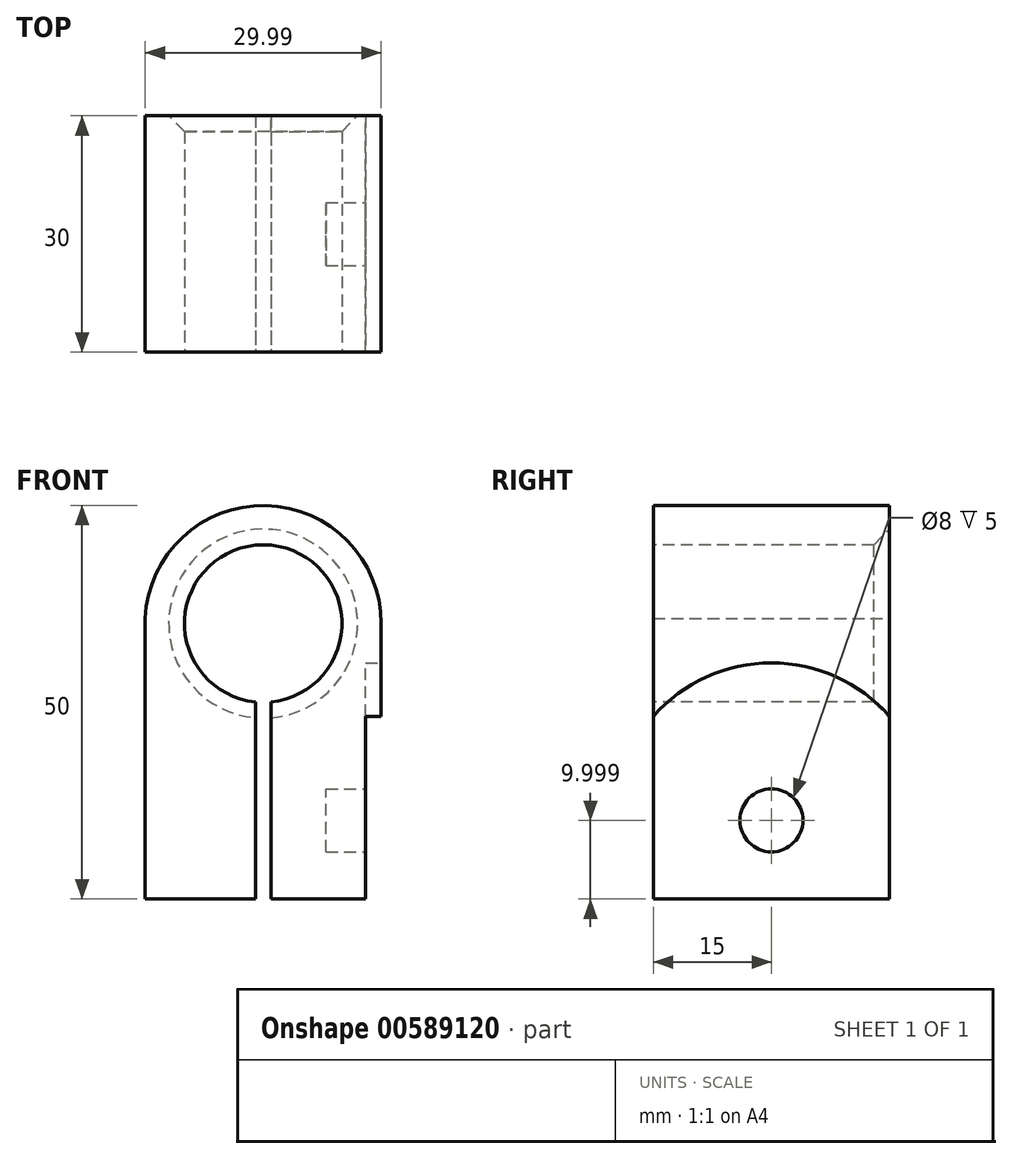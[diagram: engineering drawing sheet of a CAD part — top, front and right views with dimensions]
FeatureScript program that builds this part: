
annotation { "Feature Type Name" : "Feature", "Feature Type Description" : "" }
export const myFeature = defineFeature(function(context is Context, id is Id, definition is map)
    precondition{}
    {
        {
            var Q0;
            Q0=qCreatedBy(makeId("Front.planeOp"),FACE);
            var sketch = newSketch(context, id + "F0", { "sketchPlane" : qUnion([Q0])});
            skLineSegment(sketch, "E0", {"start": v(-14.99, -24.4) * mm, "end": v(-0.99, -24.4) * mm});
            skLineSegment(sketch, "E1", {"start": v(-24.44, 10.6) * mm, "end": v(37.77, 10.6) * mm, "construction": true});
            skLineSegment(sketch, "E2.trimOffspring", {"start": v(1, -24.4) * mm, "end": v(15, -24.4) * mm});
            skLineSegment(sketch, "E3", {"start": v(-14.99, -24.4) * mm, "end": v(-14.99, 11.27) * mm});
            skLineSegment(sketch, "E4", {"start": v(15, -24.4) * mm, "end": v(15, 10.6) * mm});
            skArc(sketch, "E5.trimOffspring", {"start": v(15, 10.6) * mm, "mid": v(0.33, 25.6) * mm, "end": v(-14.99, 11.27) * mm});
            skLineSegment(sketch, "E6", {"start": v(-0.99, -24.4) * mm, "end": v(1, -24.4) * mm});
            skSolve(sketch);
        }
        {
            var Q0;
            Q0 = qSketchRegion(id + "F0", true);
            extrude(context, id + "F1", {"entities" : qUnion([Q0]), "depth" : 30 * mm, "offsetDistance" : 25 * mm});
        }
        {
            var Q0;
            Q0=makeQuery(id+"F1.opExtrude","CAP_FACE",FACE,{"disambiguationData":[OSD([sQuery(id+"F0.wireOp",EDGE,"E0"),sQuery(id+"F0.wireOp",EDGE,"E2.trimOffspring"),sQuery(id+"F0.wireOp",EDGE,"E3"),sQuery(id+"F0.wireOp",EDGE,"E4"),sQuery(id+"F0.wireOp",EDGE,"E5.trimOffspring"),sQuery(id+"F0.wireOp",EDGE,"E6")])],"isStart":false});
            var sketch = newSketch(context, id + "F2", { "sketchPlane" : qUnion([Q0])});
            skLineSegment(sketch, "E7", {"start": v(-23.35, -24.4) * mm, "end": v(31.91, -24.4) * mm, "construction": true});
            skLineSegment(sketch, "E8", {"start": v(-20.4, 10.6) * mm, "end": v(33.94, 10.6) * mm, "construction": true});
            skLineSegment(sketch, "E9", {"start": v(0, -24.4) * mm, "end": v(0, 32.16) * mm, "construction": true});
            skCircle(sketch, "E10", {"center": v(0, 10.6) * mm, "radius": 10 * mm});
            skSolve(sketch);
        }
        {
            var Q0;
            Q0=makeQuery(id+"F2.imprint","IMPRINT",FACE,{"disambiguationData":[TD([[makeQuery(id+"F2.imprint","IMPRINT",EDGE,{"derivedFrom":sQuery(id+"F2.wireOp",EDGE,"E10")}),1.0]])]});
            extrude(context, id + "F3", {"entities" : qUnion([Q0]), "operationType" : NewBodyOperationType.REMOVE, "endBound" : BoundingType.THROUGH_ALL, "oppositeDirection" : true, "depth" : 25 * mm, "offsetDistance" : 25 * mm});
        }
        {
            var Q0;
            Q0=makeQuery(id+"F1.opExtrude","CAP_FACE",FACE,{"disambiguationData":[OSD([sQuery(id+"F0.wireOp",EDGE,"E0"),sQuery(id+"F0.wireOp",EDGE,"E2.trimOffspring"),sQuery(id+"F0.wireOp",EDGE,"E3"),sQuery(id+"F0.wireOp",EDGE,"E4"),sQuery(id+"F0.wireOp",EDGE,"E5.trimOffspring"),sQuery(id+"F0.wireOp",EDGE,"E6")])],"isStart":false});
            var sketch = newSketch(context, id + "F4", { "sketchPlane" : qUnion([Q0])});
            skLineSegment(sketch, "E11", {"start": v(0, -24.4) * mm, "end": v(-1, -24.4) * mm});
            skLineSegment(sketch, "E12", {"start": v(-1, -24.4) * mm, "end": v(-1, 0.65) * mm});
            skLineSegment(sketch, "E13", {"start": v(1, -24.4) * mm, "end": v(1, 0.65) * mm});
            skArc(sketch, "E14", {"start": v(1, 0.65) * mm, "mid": v(0, 20.6) * mm, "end": v(-1, 0.65) * mm});
            skSolve(sketch);
        }
        {
            var Q0;
            {var subQ4=sQuery(id+"F4.wireOp",EDGE,"E11");Q0=makeQuery(id+"F4.imprint","IMPRINT",FACE,{"disambiguationData":[TD([[makeQuery(id+"F4.imprint","IMPRINT",EDGE,{"derivedFrom":subQ4}),1.0]])]});}
            extrude(context, id + "F5", {"entities" : qUnion([Q0]), "operationType" : NewBodyOperationType.REMOVE, "endBound" : BoundingType.THROUGH_ALL, "oppositeDirection" : true, "depth" : 25 * mm, "offsetDistance" : 25 * mm});
        }
        {
            var Q0;
            Q0=makeQuery(id+"F1.opExtrude","SWEPT_FACE",FACE,{"disambiguationData":[OSD([sQuery(id+"F0.wireOp",EDGE,"E4")])]});
            var sketch = newSketch(context, id + "F6", { "sketchPlane" : qUnion([Q0])});
            skLineSegment(sketch, "E15", {"start": v(-30, -24.4) * mm, "end": v(-15, -24.4) * mm, "construction": true});
            skLineSegment(sketch, "E16", {"start": v(-15, -24.4) * mm, "end": v(-15, -14.4) * mm, "construction": true});
            skArc(sketch, "E17", {"start": v(0, -1.17) * mm, "mid": v(-15, 5.6) * mm, "end": v(-30, -1.17) * mm});
            skLineSegment(sketch, "E18", {"start": v(-30, -1.17) * mm, "end": v(-30, -24.4) * mm});
            skLineSegment(sketch, "E19", {"start": v(0, -24.4) * mm, "end": v(0, -1.17) * mm});
            skSolve(sketch);
        }
        {
            var Q0;
            Q0=makeQuery(id+"F6.imprint","IMPRINT",FACE,{"disambiguationData":[TD([[makeQuery(id+"F6.imprint","IMPRINT",EDGE,{"derivedFrom":sQuery(id+"F6.wireOp",EDGE,"E17")}),1.0]])]});
            extrude(context, id + "F7", {"entities" : qUnion([Q0]), "operationType" : NewBodyOperationType.REMOVE, "oppositeDirection" : true, "depth" : 2 * mm, "offsetDistance" : 25 * mm});
        }
        {
            var Q0;
            Q0=makeQuery(id+"F7.boolean.opBoolean","COPY",FACE,{"derivedFrom":makeQuery(id+"F7.opExtrude","CAP_FACE",FACE,{"disambiguationData":[OSD([sQuery(id+"F0.wireOp",EDGE,"E2.trimOffspring"),sQuery(id+"F0.wireOp",EDGE,"E4"),sQuery(id+"F6.wireOp",EDGE,"E17"),sQuery(id+"F6.wireOp",EDGE,"E18"),sQuery(id+"F6.wireOp",EDGE,"E19")])],"isStart":false})});
            var sketch = newSketch(context, id + "F8", { "sketchPlane" : qUnion([Q0])});
            skLineSegment(sketch, "E20", {"start": v(-30, -24.4) * mm, "end": v(-15, -24.4) * mm, "construction": true});
            skLineSegment(sketch, "E21", {"start": v(-15, -24.4) * mm, "end": v(-15, -14.4) * mm, "construction": true});
            skCircle(sketch, "E22", {"center": v(-15, -14.4) * mm, "radius": 4 * mm});
            skSolve(sketch);
        }
        {
            var Q0;
            Q0=makeQuery(id+"F8.imprint","IMPRINT",FACE,{"disambiguationData":[TD([[makeQuery(id+"F8.imprint","IMPRINT",EDGE,{"derivedFrom":sQuery(id+"F8.wireOp",EDGE,"E22")}),1.0]])]});
            extrude(context, id + "F9", {"entities" : qUnion([Q0]), "operationType" : NewBodyOperationType.REMOVE, "endBound" : BoundingType.SYMMETRIC, "oppositeDirection" : true, "depth" : 10 * mm, "offsetDistance" : 25 * mm});
        }
        {
            var Q0;
            Q0=makeQuery(id+"F3.boolean.opBoolean","COPY",EDGE,{"derivedFrom":makeQuery(id+"F3.opExtrude","CAP_EDGE",EDGE,{"disambiguationData":[OSD([sQuery(id+"F2.wireOp",EDGE,"E10")])],"isStart":true})});
            var Q1;
            Q1=makeQuery(id+"F3.boolean.opBoolean","INTERSECT",EDGE,{"derivedFrom":[makeQuery(id+"F1.opExtrude","CAP_FACE",FACE,{"disambiguationData":[OSD([sQuery(id+"F0.wireOp",EDGE,"E0"),sQuery(id+"F0.wireOp",EDGE,"E2.trimOffspring"),sQuery(id+"F0.wireOp",EDGE,"E3"),sQuery(id+"F0.wireOp",EDGE,"E4"),sQuery(id+"F0.wireOp",EDGE,"E5.trimOffspring"),sQuery(id+"F0.wireOp",EDGE,"E6")])],"isStart":true}),makeQuery(id+"F3.opExtrude","SWEPT_FACE",FACE,{"disambiguationData":[OSD([sQuery(id+"F2.wireOp",EDGE,"E10")])]})]});
            chamfer(context, id + "F10", {"entities" : qUnion([Q0, Q1]), "chamferType" : ChamferType.OFFSET_ANGLE, "width" : 2 * mm, "oppositeDirection" : false, "angle" : 45 * degree, "tangentPropagation" : true});
        }
    });
